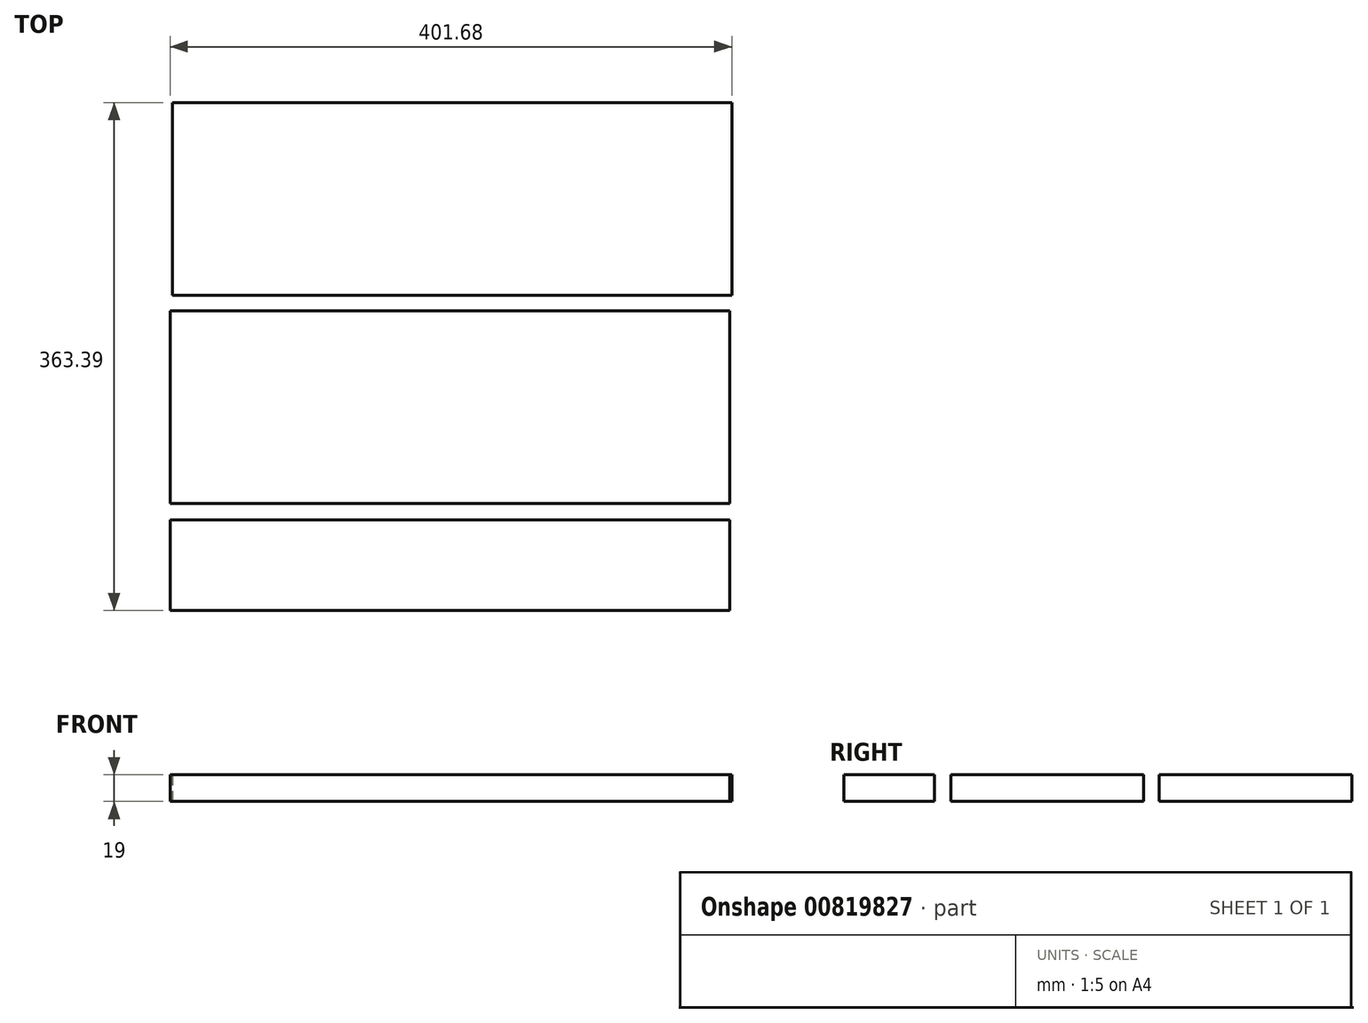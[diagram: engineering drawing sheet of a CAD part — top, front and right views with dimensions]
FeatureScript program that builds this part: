
annotation { "Feature Type Name" : "Feature", "Feature Type Description" : "" }
export const myFeature = defineFeature(function(context is Context, id is Id, definition is map)
    precondition{}
    {
        {
            var Q0;
            Q0=qCreatedBy(makeId("Top.planeOp"),FACE);
            var sketch = newSketch(context, id + "F0", { "sketchPlane" : qUnion([Q0])});
            skLineSegment(sketch, "E0.bottom", {"start": v(-327.88, 174.97) * mm, "end": v(72.12, 174.97) * mm});
            skLineSegment(sketch, "E0.top", {"start": v(-327.88, 36.97) * mm, "end": v(72.12, 36.97) * mm});
            skLineSegment(sketch, "E0.left", {"start": v(-327.88, 174.97) * mm, "end": v(-327.88, 36.97) * mm});
            skLineSegment(sketch, "E0.right", {"start": v(72.12, 174.97) * mm, "end": v(72.12, 36.97) * mm});
            skLineSegment(sketch, "E1.bottom", {"start": v(-329.31, 26.07) * mm, "end": v(70.69, 26.07) * mm});
            skLineSegment(sketch, "E1.top", {"start": v(-329.31, -111.93) * mm, "end": v(70.69, -111.93) * mm});
            skLineSegment(sketch, "E1.left", {"start": v(-329.31, 26.07) * mm, "end": v(-329.31, -111.93) * mm});
            skLineSegment(sketch, "E1.right", {"start": v(70.69, 26.07) * mm, "end": v(70.69, -111.93) * mm});
            skLineSegment(sketch, "E2.bottom", {"start": v(-329.56, -123.42) * mm, "end": v(70.44, -123.42) * mm});
            skLineSegment(sketch, "E2.top", {"start": v(-329.56, -188.42) * mm, "end": v(70.44, -188.42) * mm});
            skLineSegment(sketch, "E2.left", {"start": v(-329.56, -123.42) * mm, "end": v(-329.56, -188.42) * mm});
            skLineSegment(sketch, "E2.right", {"start": v(70.44, -123.42) * mm, "end": v(70.44, -188.42) * mm});
            skSolve(sketch);
        }
        {
            var Q0;
            Q0=makeQuery(id+"F0.imprint","IMPRINT",FACE,{"disambiguationData":[TD([[makeQuery(id+"F0.imprint","IMPRINT",EDGE,{"derivedFrom":sQuery(id+"F0.wireOp",EDGE,"E0.bottom")}),-1.0]])]});
            var Q1;
            Q1=makeQuery(id+"F0.imprint","IMPRINT",FACE,{"disambiguationData":[TD([[makeQuery(id+"F0.imprint","IMPRINT",EDGE,{"derivedFrom":sQuery(id+"F0.wireOp",EDGE,"E1.bottom")}),-1.0]])]});
            var Q2;
            Q2=makeQuery(id+"F0.imprint","IMPRINT",FACE,{"disambiguationData":[TD([[makeQuery(id+"F0.imprint","IMPRINT",EDGE,{"derivedFrom":sQuery(id+"F0.wireOp",EDGE,"E2.bottom")}),-1.0]])]});
            extrude(context, id + "F1", {"entities" : qUnion([Q0, Q1, Q2]), "depth" : 19 * mm, "offsetDistance" : 25 * mm});
        }
    });
